# Revit family: 431
name_source: partatom
category: Plumbing Fixtures
revit_build: Autodesk Revit Architecture 2012 (Build: 20110309_2315(x64)
units: mm (PartAtom-declared; Revit-internal decimal feet)

## types (1)
- 431
    1/2" heavy pattern tap washer = C-097-15
    Assembly Code = D2010
    CW Connection = Yes
    CWFU = 0
    Cost = 0 $
    Default Elevation = 0' - 0"
    Description = 2 x undertile stoptaps with 1/2"BSP female inlets + shower arm + rose
    HW Connection = Yes
    HWFU = 0
    Keynote = 1/2" heavy pattern low resistance for low pressure or high water demand installations
    Manufacturer = COBRA
    Model = 431
    Range = Star
    Shower arm = 027
    Shower head = 068BJ
    Stoptap complete = 128-15
    Stoptap sliding wall flange = C-FL30X1
    Tap headpart complete = P-32
    Type Comments = SANS 226 TYPE2
    URL = http://www.cobra.co.za
    Vent Connection = No
    WFU = 0
    Waste Connection = No

## geometry (parser evidence)
native form markers: Blend x3
no freeform markers — native parametric forms only
